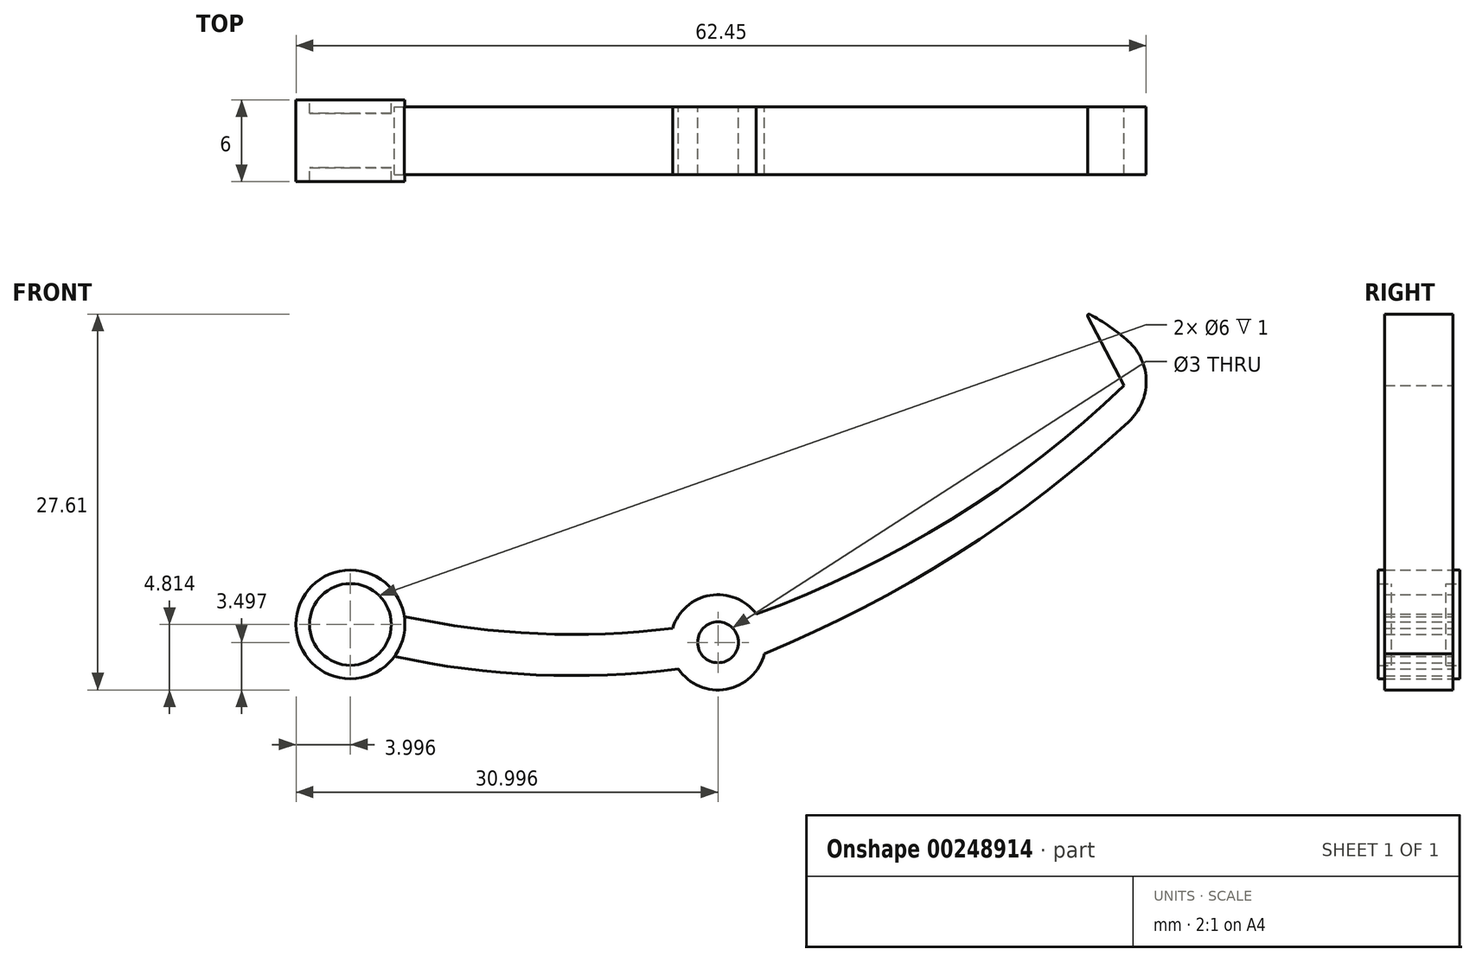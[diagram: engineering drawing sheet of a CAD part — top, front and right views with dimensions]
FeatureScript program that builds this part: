
annotation { "Feature Type Name" : "Feature", "Feature Type Description" : "" }
export const myFeature = defineFeature(function(context is Context, id is Id, definition is map)
    precondition{}
    {
        {
            var Q0;
            Q0=qCreatedBy(makeId("Front.planeOp"),FACE);
            var sketch = newSketch(context, id + "F0", { "sketchPlane" : qUnion([Q0])});
            skLineSegment(sketch, "E0", {"start": v(16.93, -54.43) * mm, "end": v(16.97, -54.42) * mm});
            skPoint(sketch, "E1.center", {"position": v(-0.03, 0) * mm});
            skLineSegment(sketch, "E2", {"start": v(0, 0) * mm, "end": v(-0.03, 0) * mm});
            skLineSegment(sketch, "E3", {"start": v(0, 71.5) * mm, "end": v(0, 66) * mm});
            skLineSegment(sketch, "E4", {"start": v(48.74, -18.05) * mm, "end": v(53.43, -19.79) * mm});
            skLineSegment(sketch, "E5", {"start": v(53.43, -19.79) * mm, "end": v(43.92, -27.8) * mm});
            skLineSegment(sketch, "E6.1.0", {"start": v(43.92, -27.8) * mm, "end": v(48.14, -30.47) * mm});
            skLineSegment(sketch, "E6.1.1", {"start": v(48.14, -30.47) * mm, "end": v(37.18, -36.33) * mm});
            skLineSegment(sketch, "E6.3.1", {"start": v(31.59, -47.43) * mm, "end": v(31.55, -47.43) * mm});
            skLineSegment(sketch, "E6.10.0", {"start": v(-40.05, -33.2) * mm, "end": v(-43.9, -36.4) * mm});
            skLineSegment(sketch, "E6.10.1", {"start": v(-43.9, -36.4) * mm, "end": v(-46.08, -24.16) * mm});
            skLineSegment(sketch, "E6.11.0", {"start": v(-46.08, -24.16) * mm, "end": v(-50.5, -26.49) * mm});
            skLineSegment(sketch, "E6.11.1", {"start": v(-50.5, -26.49) * mm, "end": v(-50.1, -14.06) * mm});
            skLineSegment(sketch, "E6.12.0", {"start": v(-50.1, -14.06) * mm, "end": v(-54.9, -15.41) * mm});
            skLineSegment(sketch, "E6.12.1", {"start": v(-54.9, -15.41) * mm, "end": v(-51.92, -3.34) * mm});
            skLineSegment(sketch, "E6.13.0", {"start": v(-51.92, -3.34) * mm, "end": v(-56.91, -3.67) * mm});
            skLineSegment(sketch, "E6.13.1", {"start": v(-56.91, -3.67) * mm, "end": v(-51.48, 7.52) * mm});
            skLineSegment(sketch, "E6.14.0", {"start": v(-51.48, 7.52) * mm, "end": v(-56.43, 8.24) * mm});
            skLineSegment(sketch, "E6.14.1", {"start": v(-56.43, 8.24) * mm, "end": v(-48.8, 18.05) * mm});
            skLineSegment(sketch, "E6.15.0", {"start": v(-48.8, 18.05) * mm, "end": v(-53.49, 19.79) * mm});
            skLineSegment(sketch, "E6.15.1", {"start": v(-53.49, 19.79) * mm, "end": v(-43.98, 27.8) * mm});
            skLineSegment(sketch, "E6.16.0", {"start": v(-43.98, 27.8) * mm, "end": v(-48.2, 30.47) * mm});
            skLineSegment(sketch, "E6.16.1", {"start": v(-48.2, 30.47) * mm, "end": v(-37.24, 36.33) * mm});
            skLineSegment(sketch, "E6.17.0", {"start": v(-37.24, 36.33) * mm, "end": v(-40.82, 39.82) * mm});
            skLineSegment(sketch, "E6.17.1", {"start": v(-40.82, 39.82) * mm, "end": v(-28.87, 43.27) * mm});
            skLineSegment(sketch, "E6.18.0", {"start": v(-28.87, 43.27) * mm, "end": v(-31.65, 47.43) * mm});
            skLineSegment(sketch, "E6.18.1", {"start": v(-31.65, 47.43) * mm, "end": v(-19.24, 48.32) * mm});
            skLineSegment(sketch, "E6.19.0", {"start": v(-19.25, 48.32) * mm, "end": v(-21.1, 52.96) * mm});
            skLineSegment(sketch, "E6.19.1", {"start": v(-21.1, 52.96) * mm, "end": v(-8.78, 51.26) * mm});
            skLineSegment(sketch, "E6.20.0", {"start": v(-8.78, 51.26) * mm, "end": v(-9.62, 56.19) * mm});
            skLineSegment(sketch, "E6.20.1", {"start": v(-9.62, 56.19) * mm, "end": v(2.07, 51.96) * mm});
            skLineSegment(sketch, "E6.21.0", {"start": v(2.07, 51.96) * mm, "end": v(2.27, 56.95) * mm});
            skLineSegment(sketch, "E6.21.1", {"start": v(2.27, 56.95) * mm, "end": v(12.83, 50.39) * mm});
            skLineSegment(sketch, "E6.22.0", {"start": v(12.82, 50.39) * mm, "end": v(14.06, 55.23) * mm});
            skLineSegment(sketch, "E6.22.1", {"start": v(14.06, 55.23) * mm, "end": v(23.02, 46.61) * mm});
            skLineSegment(sketch, "E6.23.0", {"start": v(23.02, 46.61) * mm, "end": v(25.24, 51.1) * mm});
            skLineSegment(sketch, "E6.23.1", {"start": v(25.24, 51.1) * mm, "end": v(32.2, 40.8) * mm});
            skLineSegment(sketch, "E6.24.0", {"start": v(32.2, 40.8) * mm, "end": v(35.3, 44.72) * mm});
            skLineSegment(sketch, "E6.24.1", {"start": v(35.3, 44.72) * mm, "end": v(39.99, 33.2) * mm});
            skLineSegment(sketch, "E6.25.0", {"start": v(39.99, 33.2) * mm, "end": v(43.83, 36.4) * mm});
            skLineSegment(sketch, "E6.25.1", {"start": v(43.83, 36.4) * mm, "end": v(46.02, 24.16) * mm});
            skLineSegment(sketch, "E6.26.0", {"start": v(46.02, 24.16) * mm, "end": v(50.44, 26.49) * mm});
            skLineSegment(sketch, "E6.26.1", {"start": v(50.44, 26.49) * mm, "end": v(50.03, 14.06) * mm});
            skLineSegment(sketch, "E6.27.0", {"start": v(50.03, 14.06) * mm, "end": v(54.85, 15.41) * mm});
            skLineSegment(sketch, "E6.27.1", {"start": v(54.85, 15.41) * mm, "end": v(51.86, 3.34) * mm});
            skLineSegment(sketch, "E6.28.0", {"start": v(51.86, 3.34) * mm, "end": v(56.85, 3.67) * mm});
            skLineSegment(sketch, "E6.28.1", {"start": v(56.85, 3.67) * mm, "end": v(51.42, -7.52) * mm});
            skLineSegment(sketch, "E6.29.0", {"start": v(51.42, -7.52) * mm, "end": v(56.37, -8.24) * mm});
            skLineSegment(sketch, "E6.29.1", {"start": v(56.37, -8.24) * mm, "end": v(48.74, -18.05) * mm});
            skPoint(sketch, "E7.visualSharp", {"position": v(30.07, -45.1) * mm});
            skPoint(sketch, "E8.orphan", {"position": v(-17.75, -71.35) * mm});
            skPoint(sketch, "E9.orphan", {"position": v(-12.5, -69.02) * mm});
            skLineSegment(sketch, "E10", {"start": v(-0.03, 0) * mm, "end": v(0, 0.04) * mm});
            skArc(sketch, "E11", {"start": v(35.3, 44.72) * mm, "mid": v(35.3, 44.73) * mm, "end": v(35.3, 44.73) * mm});
            skPoint(sketch, "E12.startSnap0", {"position": v(33.76, 42.76) * mm});
            skLineSegment(sketch, "E13", {"start": v(32.2, 40.8) * mm, "end": v(32.2, 40.82) * mm});
            skLineSegment(sketch, "E14.trimOffspring", {"start": v(32.2, 40.8) * mm, "end": v(35.3, 44.73) * mm});
            skPoint(sketch, "E15.orphan", {"position": v(33.76, 42.78) * mm});
            skArc(sketch, "E16", {"start": v(32.2, 40.8) * mm, "mid": v(32.49, 44.15) * mm, "end": v(31.2, 47.25) * mm});
            skArc(sketch, "E17", {"start": v(34.76, 44.04) * mm, "mid": v(34.85, 45.07) * mm, "end": v(34.72, 46.1) * mm});
            skPoint(sketch, "E18.orphan", {"position": v(0, 68.5) * mm});
            skLineSegment(sketch, "E19", {"start": v(-0.03, -659.94) * mm, "end": v(-0.03, -418) * mm, "construction": true});
            skLineSegment(sketch, "E20", {"start": v(-0.03, -637.8) * mm, "end": v(-0.03, -380.4) * mm});
            skCircle(sketch, "E21", {"center": v(-0.03, 300) * mm, "radius": 63.36 * mm});
            skLineSegment(sketch, "E22", {"start": v(-0.03, 300) * mm, "end": v(26.3, 49.53) * mm});
            skCircle(sketch, "E23", {"center": v(-2.8, -70.24) * mm, "radius": 1.5 * mm});
            skArc(sketch, "E24", {"start": v(-5.7, -72.2) * mm, "mid": v(-2.18, -73.69) * mm, "end": v(0.6, -71.08) * mm});
            skLineSegment(sketch, "E25.trimOffspring", {"start": v(19.19, -48.32) * mm, "end": v(19.18, -48.32) * mm});
            skLineSegment(sketch, "E26", {"start": v(24.22, -46) * mm, "end": v(27.04, -51.38) * mm});
            skCircle(sketch, "E27", {"center": v(-29.8, -68.93) * mm, "radius": 4 * mm});
            skArc(sketch, "E28.trimOffspring", {"start": v(0.02, -68.16) * mm, "mid": v(-3.38, -66.8) * mm, "end": v(-6.14, -69.2) * mm});
            skArc(sketch, "E29.trimOffspring", {"start": v(-25.84, -68.34) * mm, "mid": v(-16.02, -69.6) * mm, "end": v(-6.14, -69.2) * mm});
            skArc(sketch, "E30.trimOffspring", {"start": v(-26.56, -71.28) * mm, "mid": v(-16.17, -72.63) * mm, "end": v(-5.7, -72.2) * mm});
            skCircle(sketch, "E31", {"center": v(-29.8, -68.93) * mm, "radius": 3 * mm});
            skCircle(sketch, "E32", {"center": v(2.8, 69.97) * mm, "radius": 4 * mm});
            skCircle(sketch, "E33", {"center": v(2.8, 69.97) * mm, "radius": 1.5 * mm});
            skArc(sketch, "E34", {"start": v(31.2, 47.25) * mm, "mid": v(19.21, 61.05) * mm, "end": v(2.52, 68.5) * mm});
            skArc(sketch, "E35", {"start": v(34.72, 46.1) * mm, "mid": v(21.6, 62.03) * mm, "end": v(3.23, 71.41) * mm});
            skLineSegment(sketch, "E36.trimOffspring", {"start": v(28.81, -43.27) * mm, "end": v(28.81, -43.27) * mm});
            skArc(sketch, "E37", {"start": v(0.02, -68.16) * mm, "mid": v(14.4, -61.17) * mm, "end": v(27.04, -51.38) * mm});
            skArc(sketch, "E38", {"start": v(0.6, -71.08) * mm, "mid": v(16.3, -62.74) * mm, "end": v(30.03, -51.46) * mm});
            skArc(sketch, "E39", {"start": v(30.03, -51.46) * mm, "mid": v(27.54, -48.3) * mm, "end": v(24.22, -46) * mm});
            skLineSegment(sketch, "E40", {"start": v(-2.8, -70.24) * mm, "end": v(-2.8, -39.93) * mm, "construction": true});
            skLineSegment(sketch, "E41", {"start": v(24.22, -46) * mm, "end": v(-2.8, -46) * mm, "construction": true});
            skSolve(sketch);
        }
        {
            var Q0;
            Q0=makeQuery(id+"F0.imprint","IMPRINT",FACE,{"disambiguationData":[TD([[makeQuery(id+"F0.imprint","IMPRINT",EDGE,{"derivedFrom":sQuery(id+"F0.wireOp",EDGE,"E23")}),-1.0]])]});
            extrude(context, id + "F1", {"entities" : qUnion([Q0]), "endBound" : BoundingType.SYMMETRIC, "depth" : 5 * mm});
        }
        {
            var Q0;
            Q0=makeQuery(id+"F0.imprint","IMPRINT",FACE,{"disambiguationData":[TD([[makeQuery(id+"F0.imprint","IMPRINT",EDGE,{"derivedFrom":sQuery(id+"F0.wireOp",EDGE,"E31")}),-1.0]])]});
            extrude(context, id + "F2", {"entities" : qUnion([Q0]), "operationType" : NewBodyOperationType.ADD, "endBound" : BoundingType.SYMMETRIC, "depth" : 6 * mm});
        }
        {
            var Q0;
            Q0=makeQuery(id+"F0.imprint","IMPRINT",FACE,{"disambiguationData":[TD([[makeQuery(id+"F0.imprint","IMPRINT",EDGE,{"derivedFrom":sQuery(id+"F0.wireOp",EDGE,"E31")}),1.0]])]});
            extrude(context, id + "F3", {"entities" : qUnion([Q0]), "operationType" : NewBodyOperationType.ADD, "endBound" : BoundingType.SYMMETRIC, "depth" : 4 * mm});
        }
        {
            var Q0;
            Q0=makeQuery(id+"F1.opExtrude","SWEPT_EDGE",EDGE,{"disambiguationData":[OSD([sQuery(id+"F0.wireOp",EDGE,"pfDea2JD-1umd-ijTT-W1c5-PfyYZ8m9FQcx"),sQuery(id+"F0.wireOp",EDGE,"b7654b8c-4950-49b4-9a8a-22973248e8fc.trimOffspring")])]});
            var Q1;
            Q1=makeQuery(id+"F1.opExtrude","SWEPT_EDGE",EDGE,{"disambiguationData":[OSD([sQuery(id+"F0.wireOp",EDGE,"dlHR5b6y-pxCx-Ezoc-V3Qw-0JKMRhkYpIqe"),sQuery(id+"F0.wireOp",EDGE,"pfDea2JD-1umd-ijTT-W1c5-PfyYZ8m9FQcx")])]});
            var Q2;
            Q2=makeQuery(id+"F1.opExtrude","SWEPT_EDGE",EDGE,{"disambiguationData":[OSD([sQuery(id+"F0.wireOp",EDGE,"E38"),sQuery(id+"F0.wireOp",EDGE,"E39")])]});
            fillet(context, id + "F4", {"entities" : qUnion([Q0, Q1, Q2]), "radius" : 4 * mm, "tangentPropagation" : true, "allowEdgeOverflow" : false});
        }
        {
            var Q0;
            Q0=makeQuery(id+"F1.opExtrude","SWEPT_EDGE",EDGE,{"disambiguationData":[OSD([sQuery(id+"F0.wireOp",EDGE,"E26"),sQuery(id+"F0.wireOp",EDGE,"eo0D3qQ1-tSXR-QNaa-G88a-GGxUFHhM9vip"),sQuery(id+"F0.wireOp",EDGE,"E4mXm3tY-ohiX-wdYA-lBA2-cV5IMujOphFY"),sQuery(id+"F0.wireOp",EDGE,"E39")])]});
            fillet(context, id + "F5", {"entities" : qUnion([Q0]), "radius" : .1 * mm, "tangentPropagation" : true, "allowEdgeOverflow" : false});
        }
    });
